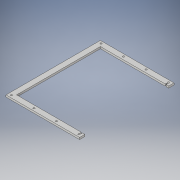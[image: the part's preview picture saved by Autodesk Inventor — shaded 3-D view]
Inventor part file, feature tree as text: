
AUTODESK INVENTOR PART (.ipt)
format: ipt  version: 2019 (Build 230136000, 136)  size: 135,680 bytes
history: native  units: mm
features: extrude x1, sketch x1
ambient origin geometry x8: Origin, YZ Plane, XZ Plane, XY Plane, X Axis, Y Axis, Z Axis, Center Point
bodies: Body1 (feature_tree)
feature tree (2):
  extrude  "Extrusion2"  Depth=22.0mm
  sketch  "Sketch2"  dims[d0=22.0mm d1=22.0mm d2=22.0mm d4=298.0mm d6=347.0mm d7=7.0mm d9=12.7mm d10=10.0mm d11=5.2mm d12=6.0mm d13=40.0mm d15=93.2mm d16=10.0mm d18=10.0mm d22=185.5mm d23=22.0mm d24=305.0mm d27=8.0mm d28=0.0mm d29=305.0mm]
